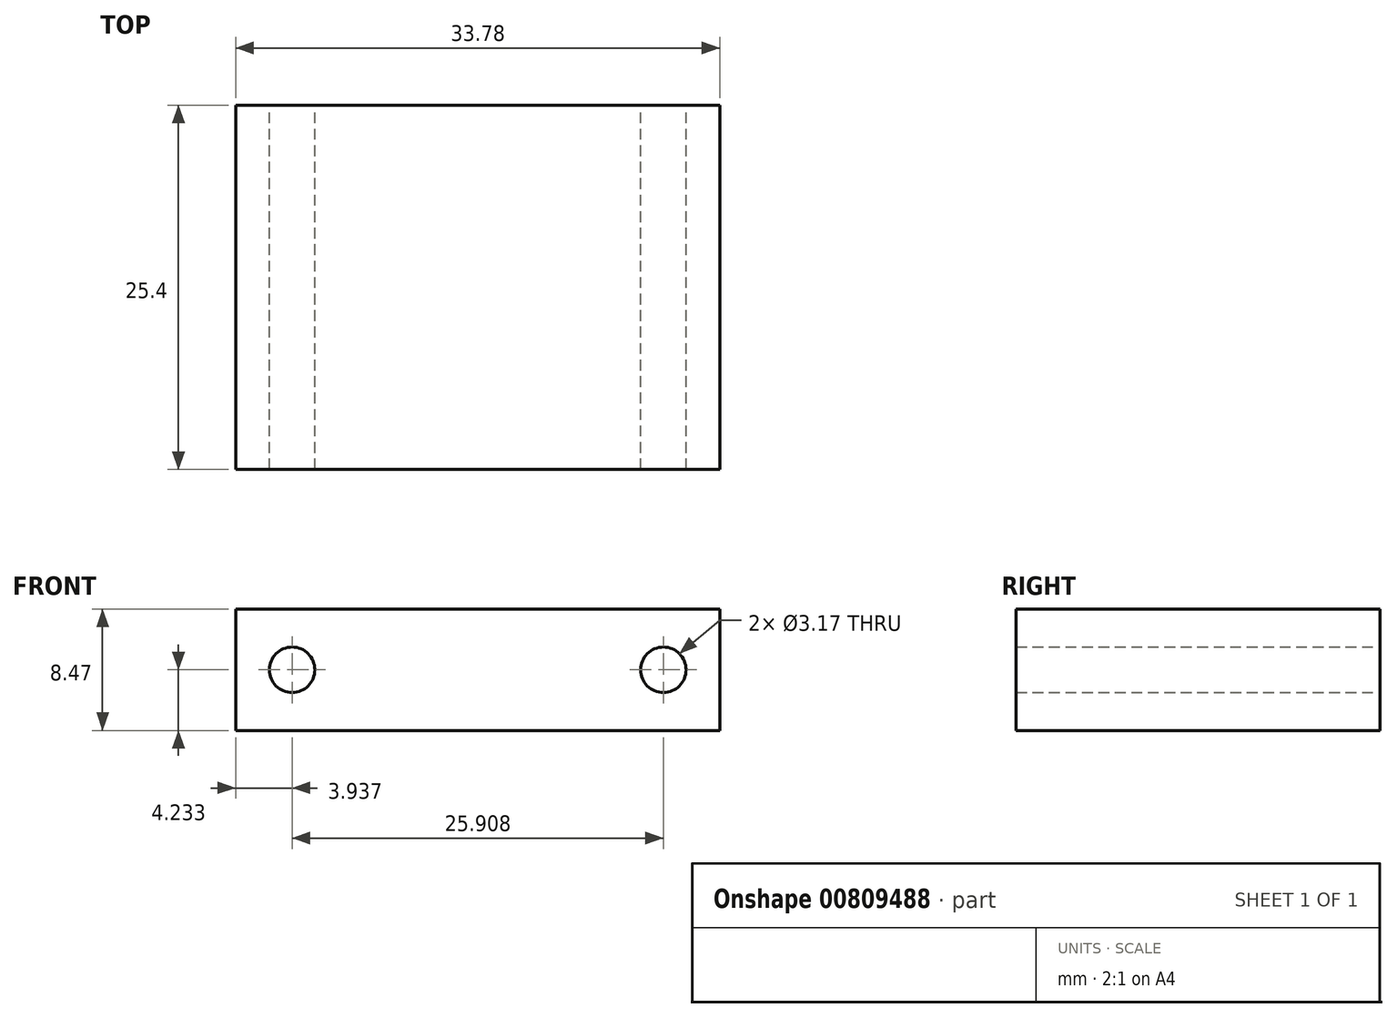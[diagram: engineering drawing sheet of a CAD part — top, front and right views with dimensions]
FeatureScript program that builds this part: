
annotation { "Feature Type Name" : "Feature", "Feature Type Description" : "" }
export const myFeature = defineFeature(function(context is Context, id is Id, definition is map)
    precondition{}
    {
        {
            var Q0;
            Q0=qCreatedBy(makeId("Front.planeOp"),FACE);
            var sketch = newSketch(context, id + "F0", { "sketchPlane" : qUnion([Q0])});
            skLineSegment(sketch, "E0.bottom", {"start": v(0, 0) * mm, "end": v(33.78, 0) * mm});
            skLineSegment(sketch, "E0.top", {"start": v(0, 8.47) * mm, "end": v(33.78, 8.47) * mm});
            skLineSegment(sketch, "E0.left", {"start": v(0, 0) * mm, "end": v(0, 8.47) * mm});
            skLineSegment(sketch, "E0.right", {"start": v(33.78, 0) * mm, "end": v(33.78, 8.47) * mm});
            skCircle(sketch, "E1", {"center": v(3.94, 4.23) * mm, "radius": 1.59 * mm});
            skPoint(sketch, "E1.centerSnap0", {"position": v(0, 4.23) * mm});
            skCircle(sketch, "E2", {"center": v(29.85, 4.23) * mm, "radius": 1.59 * mm});
            skPoint(sketch, "E2.centerSnap0", {"position": v(33.78, 4.23) * mm});
            skLineSegment(sketch, "E3", {"start": v(0, 4.23) * mm, "end": v(3.94, 4.23) * mm});
            skLineSegment(sketch, "E4", {"start": v(29.85, 4.23) * mm, "end": v(33.78, 4.23) * mm});
            skSolve(sketch);
        }
        {
            var Q0;
            Q0 = qSketchRegion(id + "F0", true);
            extrude(context, id + "F1", {"entities" : qUnion([Q0]), "depth" : 25.4 * mm, "offsetDistance" : 25.4 * mm});
        }
    });
